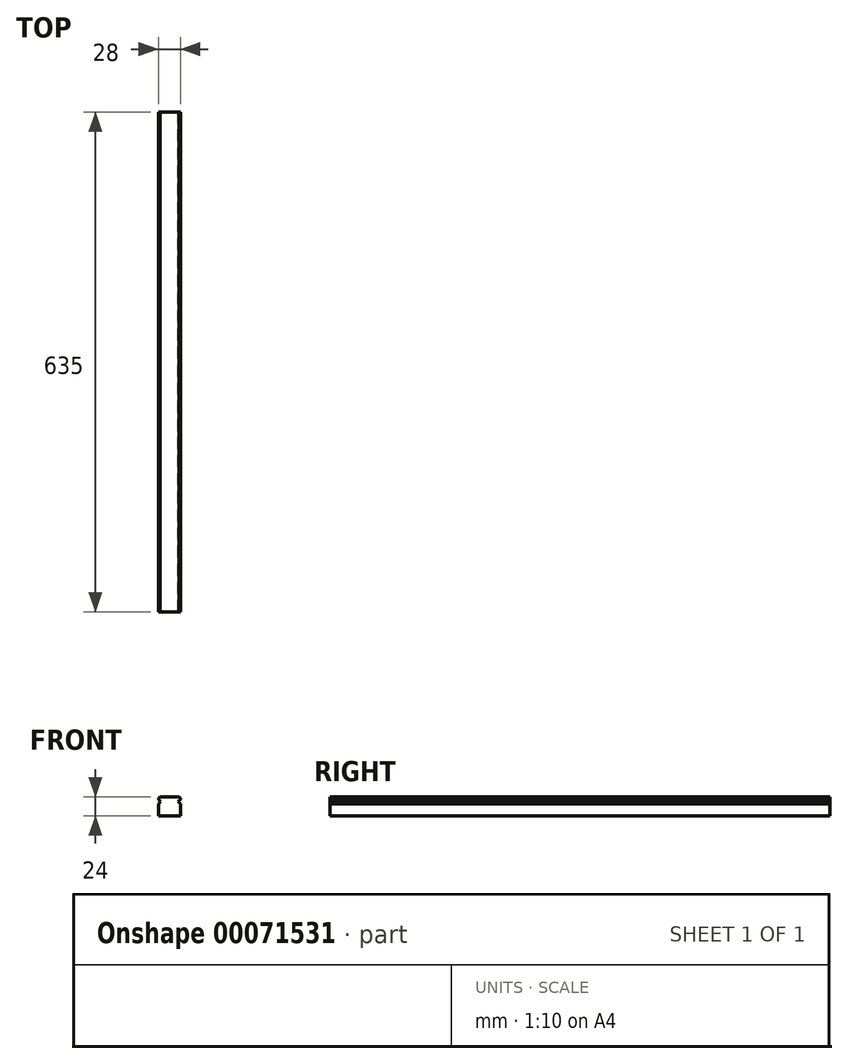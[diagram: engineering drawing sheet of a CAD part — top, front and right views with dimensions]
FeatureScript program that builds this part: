
annotation { "Feature Type Name" : "Feature", "Feature Type Description" : "" }
export const myFeature = defineFeature(function(context is Context, id is Id, definition is map)
    precondition{}
    {
        {
            var Q0;
            Q0=qCreatedBy(makeId("Front.planeOp"),FACE);
            var sketch = newSketch(context, id + "F0", { "sketchPlane" : qUnion([Q0])});
            skLineSegment(sketch, "E0.bottom", {"start": v(-9.9, 12.6) * mm, "end": v(13.87, 12.6) * mm});
            skLineSegment(sketch, "E0.top", {"start": v(-12.01, -11.4) * mm, "end": v(15.99, -11.4) * mm});
            skLineSegment(sketch, "E0.left", {"start": v(-12.01, 10.49) * mm, "end": v(-12.01, 9.49) * mm});
            skLineSegment(sketch, "E0.right", {"start": v(15.99, 10.49) * mm, "end": v(15.99, 9.49) * mm});
            skLineSegment(sketch, "E1", {"start": v(-9.9, 12.6) * mm, "end": v(-12.01, 10.49) * mm});
            skLineSegment(sketch, "E2", {"start": v(13.87, 12.6) * mm, "end": v(15.99, 10.49) * mm});
            skLineSegment(sketch, "E3", {"start": v(-12.01, 9.49) * mm, "end": v(-9.18, 6.66) * mm});
            skLineSegment(sketch, "E4", {"start": v(-9.18, 6.66) * mm, "end": v(-12.01, 3.83) * mm});
            skLineSegment(sketch, "E5", {"start": v(15.99, 9.49) * mm, "end": v(13.16, 6.66) * mm});
            skLineSegment(sketch, "E6", {"start": v(13.16, 6.66) * mm, "end": v(15.99, 3.83) * mm});
            skLineSegment(sketch, "E7.trimOffspring", {"start": v(-12.01, 3.83) * mm, "end": v(-12.01, -11.4) * mm});
            skLineSegment(sketch, "E8.trimOffspring", {"start": v(15.99, 3.83) * mm, "end": v(15.99, -11.4) * mm});
            skSolve(sketch);
        }
        {
            var Q0;
            Q0=qSketchRegion(id+"F0",true);
            extrude(context, id + "F1", {"entities" : qUnion([Q0]), "depth" : 635 * mm});
        }
    });
